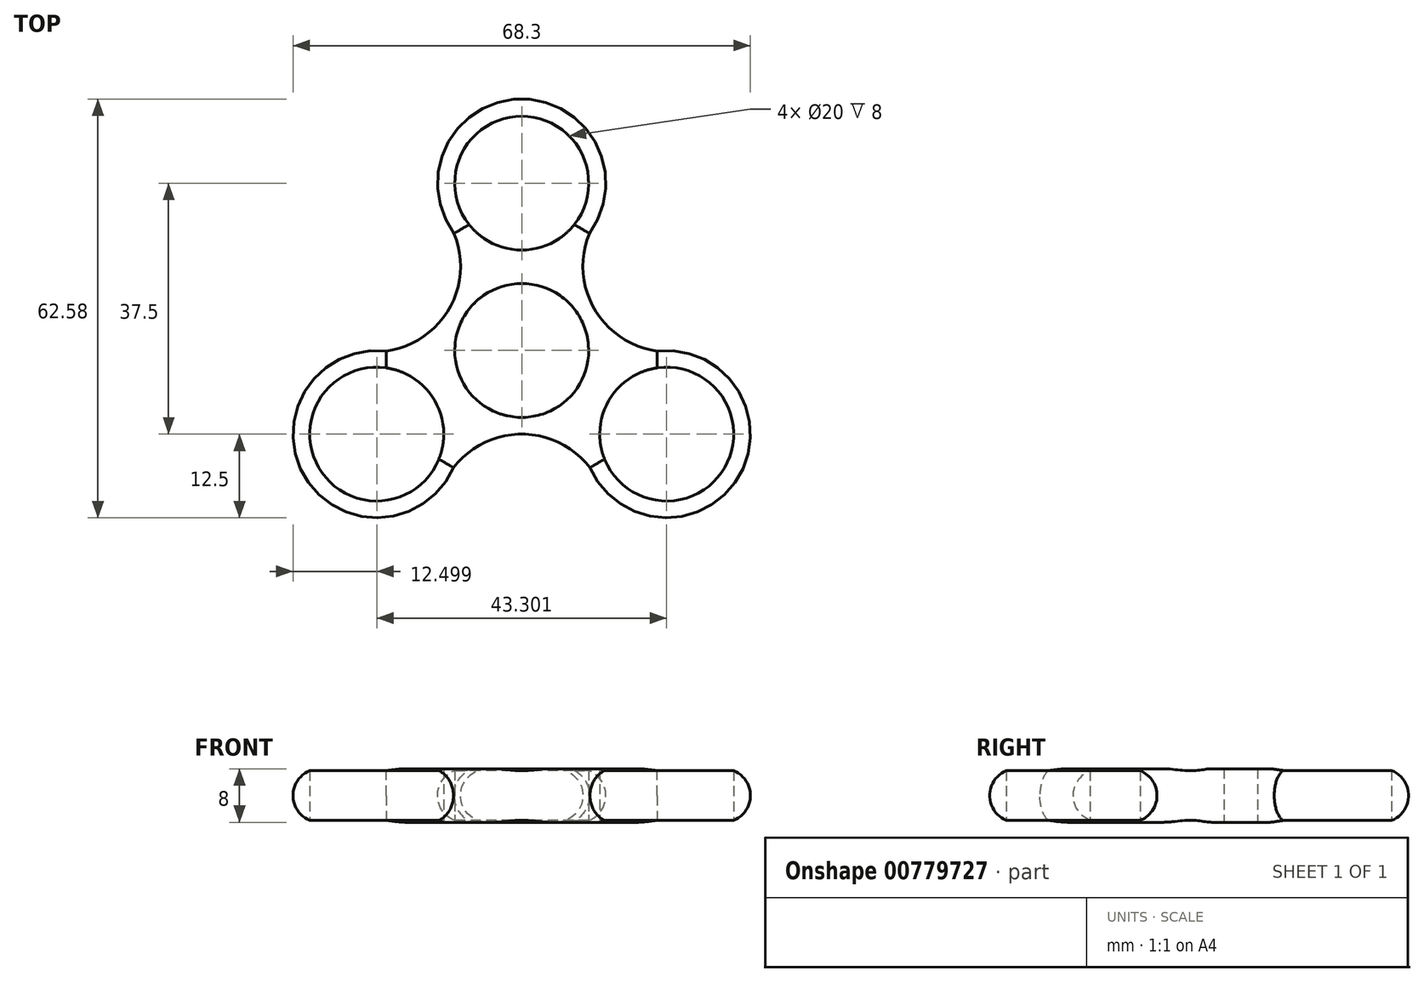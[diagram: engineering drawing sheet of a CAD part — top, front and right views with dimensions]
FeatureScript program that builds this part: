
annotation { "Feature Type Name" : "Feature", "Feature Type Description" : "" }
export const myFeature = defineFeature(function(context is Context, id is Id, definition is map)
    precondition{}
    {
        {
            var Q0;
            Q0=qCreatedBy(makeId("Top.planeOp"),FACE);
            var sketch = newSketch(context, id + "F0", { "sketchPlane" : qUnion([Q0])});
            skCircle(sketch, "E0", {"center": v(0, 0) * mm, "radius": 10 * mm});
            skCircle(sketch, "E1.cCircle", {"center": v(0, 0) * mm, "radius": 12.5 * mm, "construction": true});
            skLineSegment(sketch, "E1.0", {"start": v(21.65, -12.5) * mm, "end": v(-21.65, -12.5) * mm, "construction": true});
            skLineSegment(sketch, "E1.1", {"start": v(-21.65, -12.5) * mm, "end": v(0, 25) * mm, "construction": true});
            skLineSegment(sketch, "E1.2", {"start": v(0, 25) * mm, "end": v(21.65, -12.5) * mm, "construction": true});
            skPoint(sketch, "E1.0.midPoint", {"position": v(0, -12.5) * mm});
            skCircle(sketch, "E2", {"center": v(0, 25) * mm, "radius": 10 * mm});
            skCircle(sketch, "E3", {"center": v(21.65, -12.5) * mm, "radius": 10 * mm});
            skCircle(sketch, "E4", {"center": v(-21.65, -12.5) * mm, "radius": 10 * mm});
            skCircle(sketch, "E5", {"center": v(21.65, -12.5) * mm, "radius": 12.5 * mm});
            skCircle(sketch, "E6", {"center": v(-21.65, -12.5) * mm, "radius": 12.5 * mm});
            skCircle(sketch, "E7", {"center": v(0, 25) * mm, "radius": 12.58 * mm});
            skLineSegment(sketch, "E8", {"start": v(0, 0) * mm, "end": v(-37.05, -21.4) * mm, "construction": true});
            skLineSegment(sketch, "E9", {"start": v(-30.31, -17.5) * mm, "end": v(30.31, -17.5) * mm, "construction": true});
            skLineSegment(sketch, "E10", {"start": v(30.31, -17.5) * mm, "end": v(0, 35) * mm, "construction": true});
            skLineSegment(sketch, "E11", {"start": v(0, 35) * mm, "end": v(-30.31, -17.5) * mm, "construction": true});
            skArc(sketch, "E12", {"start": v(10.2, -17.5) * mm, "mid": v(0, -12.5) * mm, "end": v(-10.2, -17.5) * mm});
            skLineSegment(sketch, "E13", {"start": v(30.31, -17.5) * mm, "end": v(-10.83, 6.25) * mm, "construction": true});
            skArc(sketch, "E14", {"start": v(-20.25, -0.08) * mm, "mid": v(-10.85, 6.21) * mm, "end": v(-10.1, 17.5) * mm});
            skLineSegment(sketch, "E15", {"start": v(-37.05, -21.4) * mm, "end": v(10.83, 6.25) * mm, "construction": true});
            skArc(sketch, "E16", {"start": v(10.1, 17.5) * mm, "mid": v(10.85, 6.21) * mm, "end": v(20.25, -0.08) * mm});
            skSolve(sketch);
        }
        {
            var Q0;
            Q0=makeQuery(id+"F0.imprint","IMPRINT",FACE,{"disambiguationData":[TD([[makeQuery(id+"F0.imprint","IMPRINT",EDGE,{"derivedFrom":sQuery(id+"F0.wireOp",EDGE,"E2")}),-1.0]])]});
            var Q1;
            Q1=makeQuery(id+"F0.imprint","IMPRINT",FACE,{"disambiguationData":[TD([[makeQuery(id+"F0.imprint","IMPRINT",EDGE,{"derivedFrom":sQuery(id+"F0.wireOp",EDGE,"E0")}),-1.0]])]});
            var Q2;
            Q2=makeQuery(id+"F0.imprint","IMPRINT",FACE,{"disambiguationData":[TD([[makeQuery(id+"F0.imprint","IMPRINT",EDGE,{"derivedFrom":sQuery(id+"F0.wireOp",EDGE,"E4")}),-1.0]])]});
            var Q3;
            Q3=makeQuery(id+"F0.imprint","IMPRINT",FACE,{"disambiguationData":[TD([[makeQuery(id+"F0.imprint","IMPRINT",EDGE,{"derivedFrom":sQuery(id+"F0.wireOp",EDGE,"E3")}),-1.0]])]});
            extrude(context, id + "F1", {"entities" : qUnion([Q0, Q1, Q2, Q3]), "depth" : 8 * mm, "offsetDistance" : 25 * mm});
        }
        {
            var Q0;
            Q0=makeQuery(id+"F1.opExtrude","CAP_EDGE",EDGE,{"disambiguationData":[OSD([sQuery(id+"F0.wireOp",EDGE,"E6")])],"isStart":false});
            var Q1;
            Q1=makeQuery(id+"F1.opExtrude","CAP_EDGE",EDGE,{"disambiguationData":[OSD([sQuery(id+"F0.wireOp",EDGE,"E12")])],"isStart":false});
            var Q2;
            Q2=makeQuery(id+"F1.opExtrude","CAP_EDGE",EDGE,{"disambiguationData":[OSD([sQuery(id+"F0.wireOp",EDGE,"E14")])],"isStart":false});
            var Q3;
            Q3=makeQuery(id+"F1.opExtrude","CAP_EDGE",EDGE,{"disambiguationData":[OSD([sQuery(id+"F0.wireOp",EDGE,"E16")])],"isStart":false});
            var Q4;
            Q4=makeQuery(id+"F1.opExtrude","CAP_EDGE",EDGE,{"disambiguationData":[OSD([sQuery(id+"F0.wireOp",EDGE,"E5")])],"isStart":false});
            var Q5;
            Q5=makeQuery(id+"F1.opExtrude","CAP_EDGE",EDGE,{"disambiguationData":[OSD([sQuery(id+"F0.wireOp",EDGE,"E7")])],"isStart":false});
            fillet(context, id + "F2", {"entities" : qUnion([Q0, Q1, Q2, Q3, Q4, Q5]), "radius" : 4 * mm, "tangentPropagation" : true, "allowEdgeOverflow" : false});
        }
        {
            var Q0;
            Q0=makeQuery(id+"F1.opExtrude","CAP_EDGE",EDGE,{"disambiguationData":[OSD([sQuery(id+"F0.wireOp",EDGE,"E5")])],"isStart":true});
            var Q1;
            Q1=makeQuery(id+"F1.opExtrude","CAP_EDGE",EDGE,{"disambiguationData":[OSD([sQuery(id+"F0.wireOp",EDGE,"E12")])],"isStart":true});
            var Q2;
            Q2=makeQuery(id+"F1.opExtrude","CAP_EDGE",EDGE,{"disambiguationData":[OSD([sQuery(id+"F0.wireOp",EDGE,"E16")])],"isStart":true});
            var Q3;
            Q3=makeQuery(id+"F1.opExtrude","CAP_EDGE",EDGE,{"disambiguationData":[OSD([sQuery(id+"F0.wireOp",EDGE,"E7")])],"isStart":true});
            var Q4;
            Q4=makeQuery(id+"F1.opExtrude","CAP_EDGE",EDGE,{"disambiguationData":[OSD([sQuery(id+"F0.wireOp",EDGE,"E14")])],"isStart":true});
            var Q5;
            Q5=makeQuery(id+"F1.opExtrude","CAP_EDGE",EDGE,{"disambiguationData":[OSD([sQuery(id+"F0.wireOp",EDGE,"E6")])],"isStart":true});
            fillet(context, id + "F3", {"entities" : qUnion([Q0, Q1, Q2, Q3, Q4, Q5]), "radius" : 4 * mm, "tangentPropagation" : true, "allowEdgeOverflow" : false});
        }
    });
